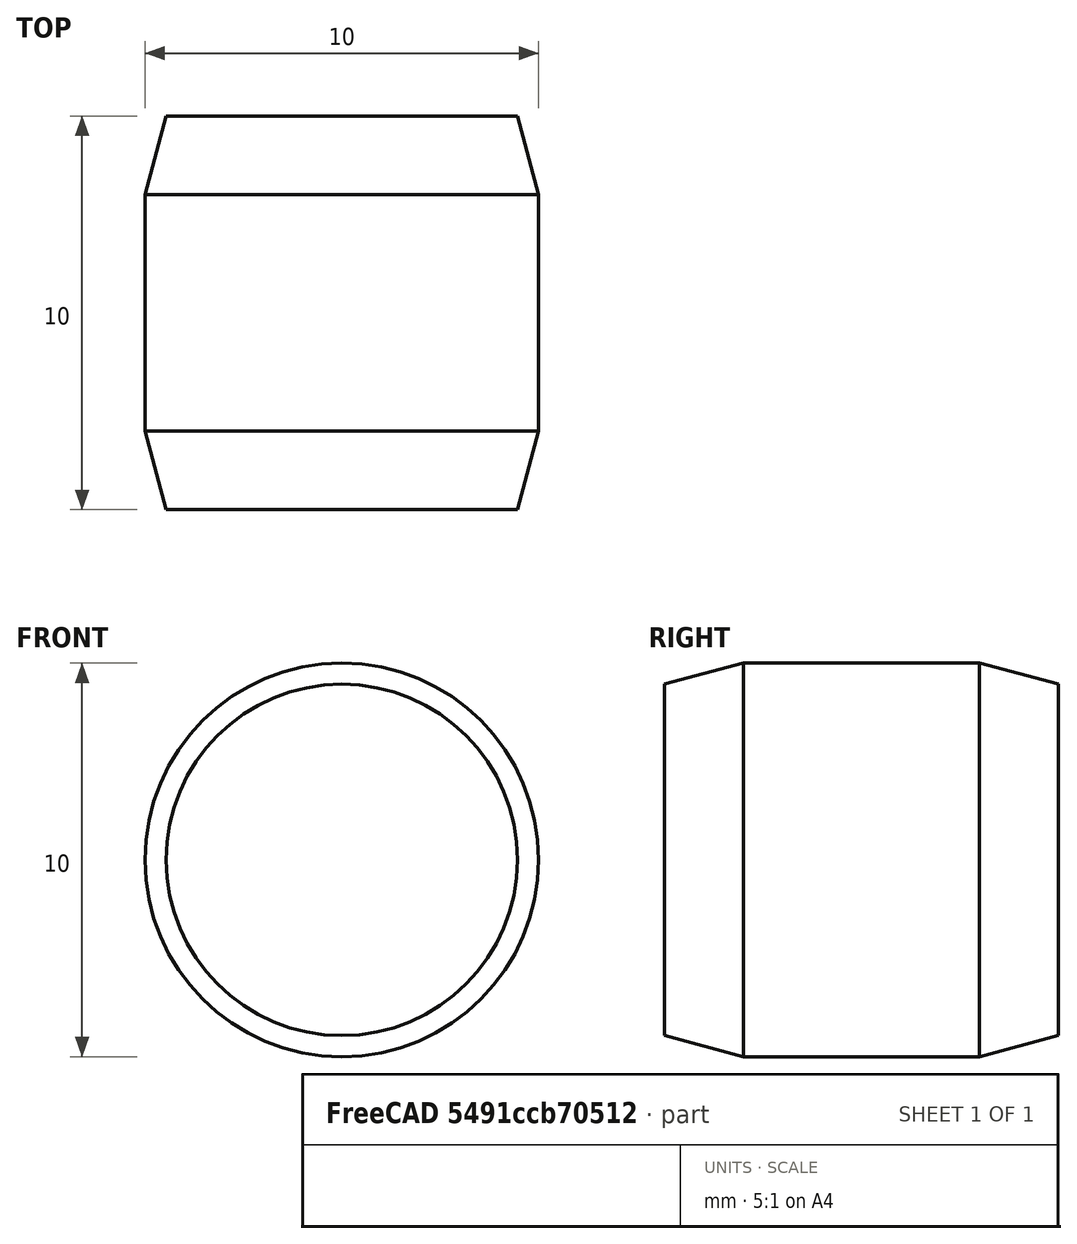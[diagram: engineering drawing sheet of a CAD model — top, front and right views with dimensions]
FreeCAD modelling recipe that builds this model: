
FCSTD DOCUMENT  (FreeCAD 0.15R4470 (Git))
Label: Zyl-Stift_ISO_2338-10x10
License: CC-BY 3.0
LicenseURL: http://creativecommons.org/licenses/by/3.0/
objects: Sketcher::SketchObject×1, PartDesign::Revolution×1
note: 3 computed .brp shape members not serialized (recipe doc carries the construction recipe); baked Part::Feature solids carry a one-line shape summary decoded from their .brp

FEATURE [Sketcher::SketchObject] Sketch
  Placement = pos=(0,0,0) rot=(0.57735,0.57735,0.57735;2.0944rad)
  sketch-geometry (7):
    g0: LineSegment StartX=0 StartY=0 StartZ=0 EndX=0 EndY=4.4641 EndZ=0
    g1: LineSegment StartX=0 StartY=4.4641 StartZ=0 EndX=2 EndY=5 EndZ=0
    g2: LineSegment StartX=2 StartY=5 StartZ=0 EndX=8 EndY=5 EndZ=0
    g3: LineSegment StartX=8 StartY=5 StartZ=0 EndX=10 EndY=4.4641 EndZ=0
    g4: LineSegment StartX=10 StartY=4.4641 StartZ=0 EndX=10 EndY=0 EndZ=0
    g5: LineSegment StartX=10 StartY=0 StartZ=0 EndX=0 EndY=0 EndZ=0
    g6: LineSegment [constr] StartX=0 StartY=4.4641 StartZ=0 EndX=10 EndY=4.4641 EndZ=0
  constraints (19):
    c: Coincident(g0,g-1)
    c: PointOnObject(g0,g-2)
    c: Coincident(g0,g1)
    c: Coincident(g1,g2)
    c: Horizontal(g2)
    c: Coincident(g2,g3)
    c: Coincident(g3,g4)
    c: Vertical(g4)
    c: Coincident(g4,g5)
    c: Coincident(g5,g-1)
    c: Horizontal(g5)
    c: Equal(g3,g1)
    c: Coincident(g6,g0)
    c: Coincident(g6,g3)
    c: Horizontal(g6)
    c: Angle(g6,g1) = 0.261799
    c: DistanceY(g-1,g1) = 5
    c: DistanceX(g5) = -10
    c: DistanceX(g1) = 2
FEATURE [PartDesign::Revolution] Revolution  label="Zyl-Stift ISO 2338-10x10 #"
  Angle = 360
  Axis = (0,1,0)
  Base = (0,0,0)
  Placement = pos=(0,0,0) rot=(0.57735,0.57735,0.57735;2.0944rad)
  ReferenceAxis = -> Sketch [H_Axis]
  Sketch = -> Sketch
